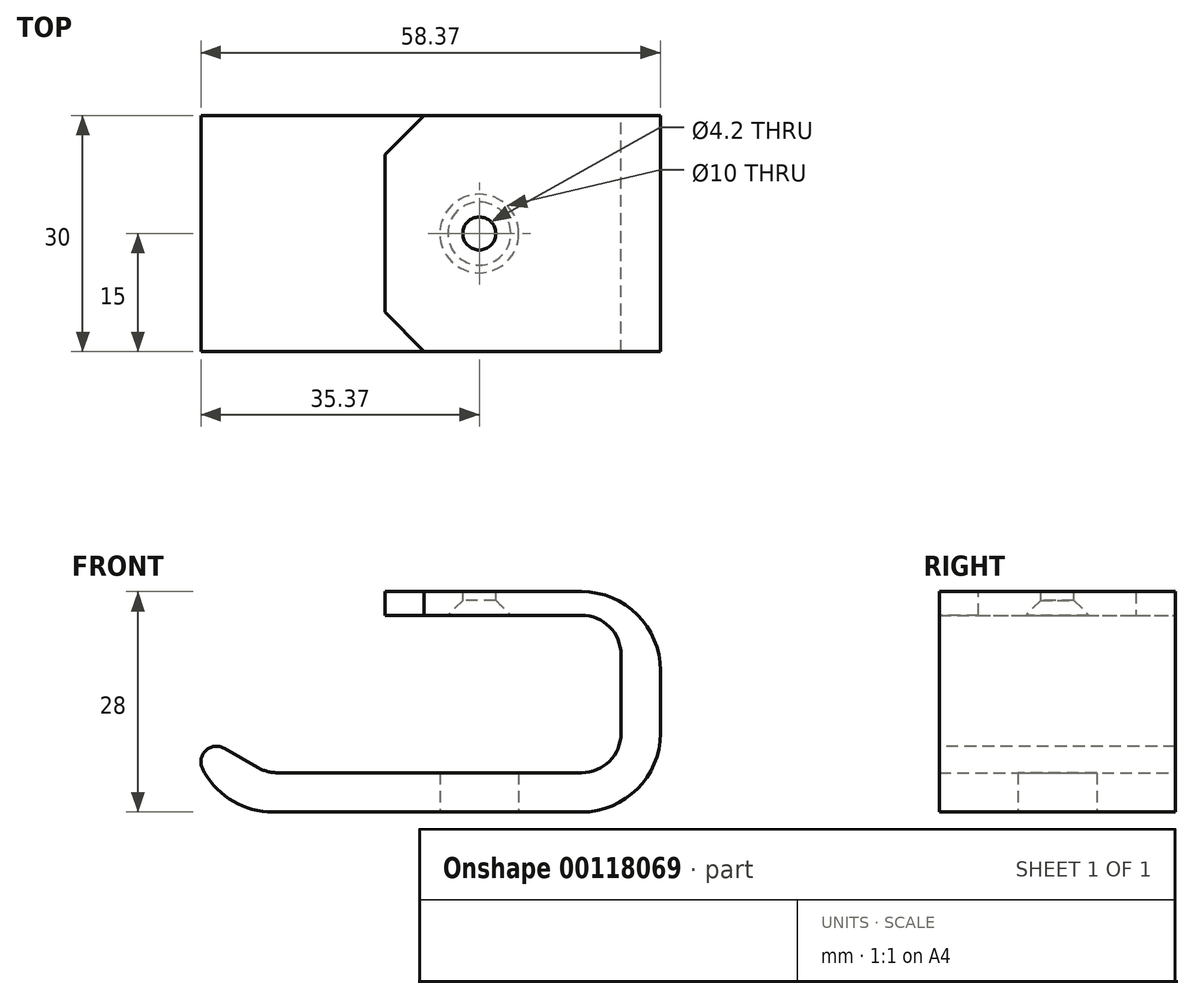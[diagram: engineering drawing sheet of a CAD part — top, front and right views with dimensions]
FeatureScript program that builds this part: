
annotation { "Feature Type Name" : "Feature", "Feature Type Description" : "" }
export const myFeature = defineFeature(function(context is Context, id is Id, definition is map)
    precondition{}
    {
        {
            var Q0;
            Q0=qCreatedBy(makeId("Front.planeOp"),FACE);
            var sketch = newSketch(context, id + "F0", { "sketchPlane" : qUnion([Q0])});
            skLineSegment(sketch, "E0", {"start": v(0, 0) * mm, "end": v(30, 0) * mm});
            skLineSegment(sketch, "E1", {"start": v(30, 0) * mm, "end": v(30, -20) * mm});
            skLineSegment(sketch, "E2", {"start": v(30, -20) * mm, "end": v(-15, -20) * mm});
            skLineSegment(sketch, "E3", {"start": v(-15, -20) * mm, "end": v(-23.66, -15) * mm});
            skLineSegment(sketch, "E4", {"start": v(0, 0) * mm, "end": v(0, 3) * mm});
            skLineSegment(sketch, "E5", {"start": v(0, 3) * mm, "end": v(35, 3) * mm});
            skLineSegment(sketch, "E6", {"start": v(35, 3) * mm, "end": v(35, -25) * mm});
            skLineSegment(sketch, "E7", {"start": v(35, -25) * mm, "end": v(-20, -25) * mm});
            skLineSegment(sketch, "E8", {"start": v(-20, -25) * mm, "end": v(-25.08, -16.2) * mm});
            skLineSegment(sketch, "E9", {"start": v(-25.08, -16.2) * mm, "end": v(-23.66, -15) * mm});
            skSolve(sketch);
        }
        {
            var Q0;
            Q0=makeQuery(id+"F0.imprint","IMPRINT",FACE,{"disambiguationData":[TD([[makeQuery(id+"F0.imprint","IMPRINT",EDGE,{"derivedFrom":sQuery(id+"F0.wireOp",EDGE,"E0")}),1.0]])]});
            extrude(context, id + "F1", {"entities" : qUnion([Q0]), "depth" : 30 * mm, "symmetric" : true});
        }
        {
            var Q0;
            Q0=makeQuery(id+"F1.opExtrude","SWEPT_EDGE",EDGE,{"disambiguationData":[OSD([sQuery(id+"F0.wireOp",EDGE,"E0"),sQuery(id+"F0.wireOp",EDGE,"E1")])]});
            var Q1;
            Q1=makeQuery(id+"F1.opExtrude","SWEPT_EDGE",EDGE,{"disambiguationData":[OSD([sQuery(id+"F0.wireOp",EDGE,"E1"),sQuery(id+"F0.wireOp",EDGE,"E2")])]});
            var Q2;
            Q2=makeQuery(id+"F1.opExtrude","SWEPT_EDGE",EDGE,{"disambiguationData":[OSD([sQuery(id+"F0.wireOp",EDGE,"E2"),sQuery(id+"F0.wireOp",EDGE,"E3")])]});
            fillet(context, id + "F2", {"entities" : qUnion([Q0, Q1, Q2]), "radius" : 5 * mm, "tangentPropagation" : true, "allowEdgeOverflow" : false});
        }
        {
            var Q0;
            Q0=makeQuery(id+"F1.opExtrude","SWEPT_EDGE",EDGE,{"disambiguationData":[OSD([sQuery(id+"F0.wireOp",EDGE,"E5"),sQuery(id+"F0.wireOp",EDGE,"E6")])]});
            var Q1;
            Q1=makeQuery(id+"F1.opExtrude","SWEPT_EDGE",EDGE,{"disambiguationData":[OSD([sQuery(id+"F0.wireOp",EDGE,"E6"),sQuery(id+"F0.wireOp",EDGE,"E7")])]});
            var Q2;
            Q2=makeQuery(id+"F1.opExtrude","SWEPT_EDGE",EDGE,{"disambiguationData":[OSD([sQuery(id+"F0.wireOp",EDGE,"E7"),sQuery(id+"F0.wireOp",EDGE,"E8")])]});
            fillet(context, id + "F3", {"entities" : qUnion([Q0, Q1, Q2]), "radius" : 10 * mm, "tangentPropagation" : true, "allowEdgeOverflow" : false});
        }
        {
            var Q0;
            Q0=makeQuery(id+"F1.opExtrude","SWEPT_FACE",FACE,{"disambiguationData":[OSD([sQuery(id+"F0.wireOp",EDGE,"E0")])]});
            var sketch = newSketch(context, id + "F4", { "sketchPlane" : qUnion([Q0])});
            skCircle(sketch, "E10", {"center": v(12, 0) * mm, "radius": 2.1 * mm});
            skSolve(sketch);
        }
        {
            var Q0;
            Q0=sQuery(id+"F4.wireOp",VERTEX,"E10.center");
            var Q1;
            Q1=makeQuery(id+"F1.opExtrude","SWEPT_BODY",BODY,{"disambiguationData":[OSD([sQuery(id+"F0.wireOp",EDGE,"E0"),sQuery(id+"F0.wireOp",EDGE,"E1"),sQuery(id+"F0.wireOp",EDGE,"E2"),sQuery(id+"F0.wireOp",EDGE,"E3"),sQuery(id+"F0.wireOp",EDGE,"E4"),sQuery(id+"F0.wireOp",EDGE,"E5"),sQuery(id+"F0.wireOp",EDGE,"E6"),sQuery(id+"F0.wireOp",EDGE,"E7"),sQuery(id+"F0.wireOp",EDGE,"E8"),sQuery(id+"F0.wireOp",EDGE,"E9")])]});
            hole(context, id + "F5", {"style" : HoleStyle.C_SINK, "endStyle" : HoleEndStyle.THROUGH, "holeDiameter" : 4.2 * mm, "cSinkDiameter" : 8 * mm, "cSinkAngle" : 90 * degree, "locations" : qUnion([Q0]), "scope" : qUnion([Q1]), "isTappedThrough" : true, "startStyle" : HoleStartStyle.PART});
        }
        {
            var Q0;
            Q0=makeQuery(id+"F1.opExtrude","SWEPT_FACE",FACE,{"disambiguationData":[OSD([sQuery(id+"F0.wireOp",EDGE,"E7")])]});
            var sketch = newSketch(context, id + "F6", { "sketchPlane" : qUnion([Q0])});
            skCircle(sketch, "E11.0", {"center": v(12, 0) * mm, "radius": 4 * mm, "construction": true});
            skCircle(sketch, "E12", {"center": v(12, 0) * mm, "radius": 5 * mm});
            skSolve(sketch);
        }
        {
            var Q0;
            Q0=makeQuery(id+"F6.imprint","IMPRINT",FACE,{"disambiguationData":[TD([[makeQuery(id+"F6.imprint","IMPRINT",EDGE,{"derivedFrom":sQuery(id+"F6.wireOp",EDGE,"E12")}),1.0]])]});
            extrude(context, id + "F7", {"entities" : qUnion([Q0]), "operationType" : NewBodyOperationType.REMOVE, "endBound" : BoundingType.UP_TO_NEXT, "oppositeDirection" : true, "depth" : 25 * mm});
        }
        {
            var Q0;
            Q0=makeQuery(id+"F1.opExtrude","SWEPT_EDGE",EDGE,{"disambiguationData":[OSD([sQuery(id+"F0.wireOp",EDGE,"E8"),sQuery(id+"F0.wireOp",EDGE,"E9")])]});
            fillet(context, id + "F8", {"entities" : qUnion([Q0]), "radius" : 5 * mm, "tangentPropagation" : true, "allowEdgeOverflow" : false});
        }
        {
            var Q0;
            Q0=makeQuery(id+"F8.opFillet","BLEND_EDGE",EDGE,{"blendedFrom":[makeQuery(id+"F1.opExtrude","SWEPT_EDGE",EDGE,{"disambiguationData":[OSD([sQuery(id+"F0.wireOp",EDGE,"E8"),sQuery(id+"F0.wireOp",EDGE,"E9")])]}),makeQuery(id+"F1.opExtrude","SWEPT_FACE",FACE,{"disambiguationData":[OSD([sQuery(id+"F0.wireOp",EDGE,"E3")])]})],"blendedInto":[makeQuery(id+"F1.opExtrude","SWEPT_FACE",FACE,{"disambiguationData":[OSD([sQuery(id+"F0.wireOp",EDGE,"E3")])]})]});
            fillet(context, id + "F9", {"entities" : qUnion([Q0]), "radius" : 2 * mm, "tangentPropagation" : true, "allowEdgeOverflow" : false});
        }
        {
            var Q0;
            Q0=makeQuery(id+"F1.opExtrude","CAP_EDGE",EDGE,{"disambiguationData":[OSD([sQuery(id+"F0.wireOp",EDGE,"E4")])],"isStart":true});
            var Q1;
            Q1=makeQuery(id+"F1.opExtrude","CAP_EDGE",EDGE,{"disambiguationData":[OSD([sQuery(id+"F0.wireOp",EDGE,"E4")])],"isStart":false});
            chamfer(context, id + "F10", {"entities" : qUnion([Q0, Q1]), "width" : 5 * mm, "tangentPropagation" : true});
        }
    });
